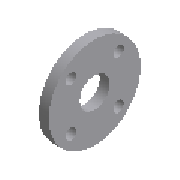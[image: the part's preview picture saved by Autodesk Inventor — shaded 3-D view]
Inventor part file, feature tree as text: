
AUTODESK INVENTOR PART (.ipt)
format: ipt  version: 2025 (Build 290162010, 162A)  size: 169,472 bytes
history: native  units: mm (DEFAULTED — no unit token found)
features: other x6, revolve x1, extrude x1, pattern_circular x1
ambient origin geometry x8: Origin, YZ Plane, XZ Plane, XY Plane, X Axis, Y Axis, Z Axis, Center Point
bodies: Solid1 (feature_tree)
feature tree (9):
  other  "DIN EN 1092-1 Plate Flange for Welding Type 01 - PN 25 150 x 168.3"
  revolve  "Revolution1"  Angle=90.0deg
  extrude  "Extrusion1"  Depth=300.0mm
  pattern_circular  "Circular Pattern1"  Count=3  [1 undecoded]
  other  "Work Axis1"
  other  "Work Point1"
  other  "Work Axis2"
  other  "Work Point2"
  other  "Work Point3"
note: 1 required parameter value undecoded (feature->parameter linkage not recoverable at this tier; creation-order binding heuristic only, values carry confidence <= 0.55)
